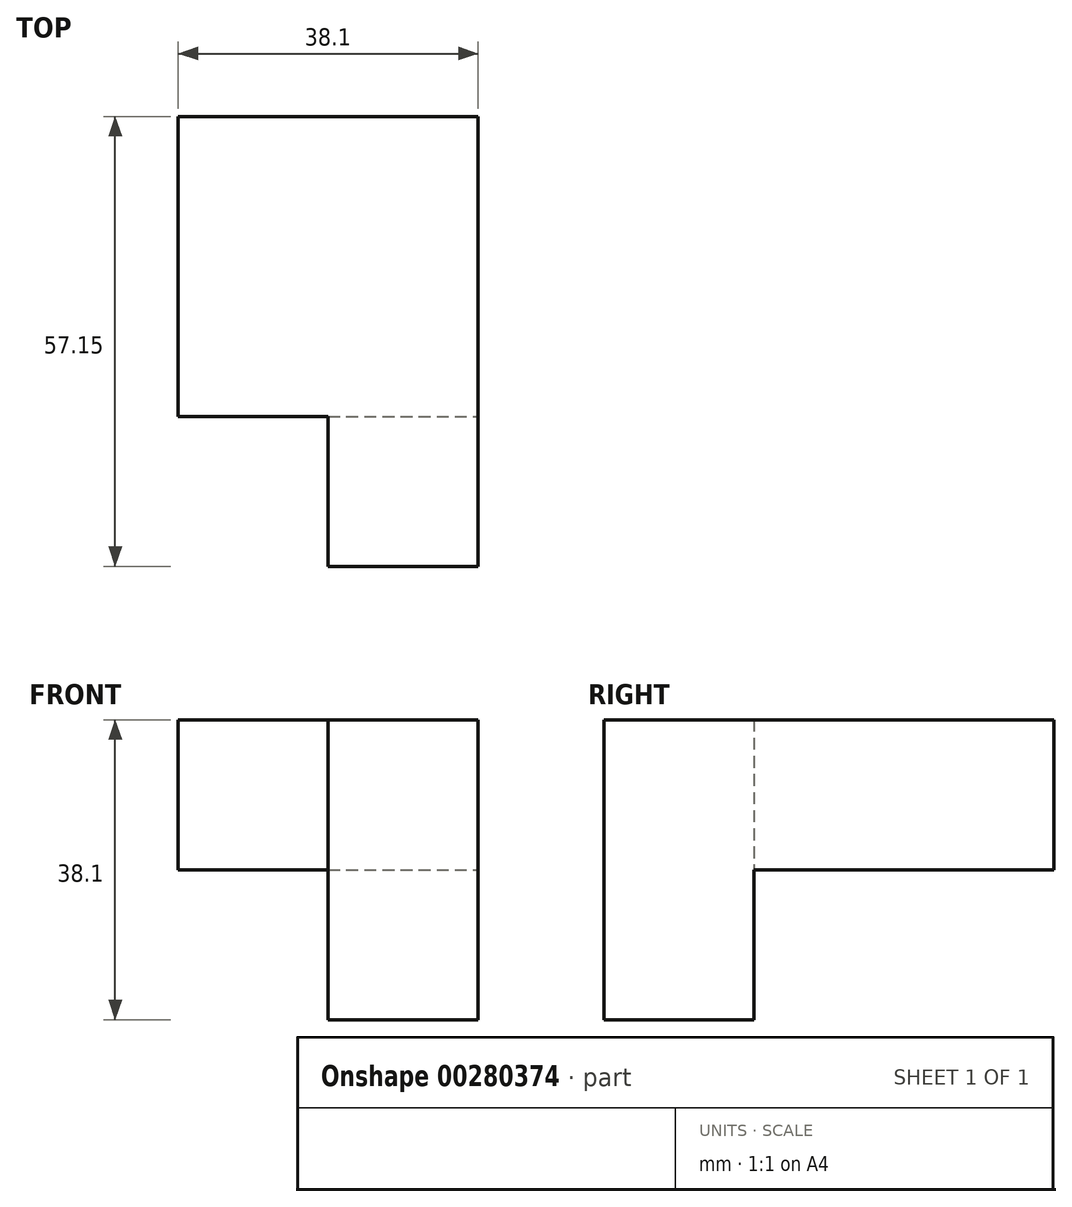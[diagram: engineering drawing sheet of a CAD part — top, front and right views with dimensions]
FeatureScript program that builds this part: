
annotation { "Feature Type Name" : "Feature", "Feature Type Description" : "" }
export const myFeature = defineFeature(function(context is Context, id is Id, definition is map)
    precondition{}
    {
        {
            var Q0;
            Q0=qCreatedBy(makeId("Top.planeOp"),FACE);
            var sketch = newSketch(context, id + "F0", { "sketchPlane" : qUnion([Q0])});
            skLineSegment(sketch, "E0.bottom", {"start": v(0, 0) * mm, "end": v(38.1, 0) * mm});
            skLineSegment(sketch, "E0.top", {"start": v(0, 38.1) * mm, "end": v(38.1, 38.1) * mm});
            skLineSegment(sketch, "E0.left", {"start": v(0, 0) * mm, "end": v(0, 38.1) * mm});
            skLineSegment(sketch, "E0.right", {"start": v(38.1, 0) * mm, "end": v(38.1, 38.1) * mm});
            skSolve(sketch);
        }
        {
            var Q0;
            Q0 = qSketchRegion(id + "F0", true);
            extrude(context, id + "F1", {"entities" : qUnion([Q0]), "depth" : 19.05 * mm});
        }
        {
            var Q0;
            Q0=makeQuery(id+"F1.opExtrude","SWEPT_FACE",FACE,{"disambiguationData":[OSD([sQuery(id+"F0.wireOp",EDGE,"E0.bottom")])]});
            var sketch = newSketch(context, id + "F2", { "sketchPlane" : qUnion([Q0])});
            skLineSegment(sketch, "E1.bottom", {"start": v(38.1, 19.05) * mm, "end": v(19.05, 19.05) * mm});
            skLineSegment(sketch, "E1.top", {"start": v(38.1, 0) * mm, "end": v(19.05, 0) * mm});
            skLineSegment(sketch, "E1.left", {"start": v(38.1, 19.05) * mm, "end": v(38.1, 0) * mm});
            skLineSegment(sketch, "E1.right", {"start": v(19.05, 19.05) * mm, "end": v(19.05, 0) * mm});
            skSolve(sketch);
        }
        {
            var Q0;
            Q0 = qSketchRegion(id + "F2", true);
            extrude(context, id + "F3", {"entities" : qUnion([Q0]), "operationType" : NewBodyOperationType.ADD, "depth" : 19.05 * mm});
        }
        {
            var Q0;
            Q0=makeQuery(id+"F3.boolean.opBoolean","MERGE",FACE,{"derivedFrom":[makeQuery(id+"F1.opExtrude","CAP_FACE",FACE,{"disambiguationData":[OSD([sQuery(id+"F0.wireOp",EDGE,"E0.bottom"),sQuery(id+"F0.wireOp",EDGE,"E0.top"),sQuery(id+"F0.wireOp",EDGE,"E0.left"),sQuery(id+"F0.wireOp",EDGE,"E0.right")])],"isStart":true}),makeQuery(id+"F3.opExtrude","SWEPT_FACE",FACE,{"disambiguationData":[OSD([sQuery(id+"F2.wireOp",EDGE,"E1.top")])]})]});
            var sketch = newSketch(context, id + "F4", { "sketchPlane" : qUnion([Q0])});
            skLineSegment(sketch, "E2.bottom", {"start": v(19.05, 19.05) * mm, "end": v(38.1, 19.05) * mm});
            skLineSegment(sketch, "E2.top", {"start": v(19.05, 0) * mm, "end": v(38.1, 0) * mm});
            skLineSegment(sketch, "E2.left", {"start": v(19.05, 19.05) * mm, "end": v(19.05, 0) * mm});
            skLineSegment(sketch, "E2.right", {"start": v(38.1, 19.05) * mm, "end": v(38.1, 0) * mm});
            skSolve(sketch);
        }
        {
            var Q0;
            Q0 = qSketchRegion(id + "F4", true);
            extrude(context, id + "F5", {"entities" : qUnion([Q0]), "operationType" : NewBodyOperationType.ADD, "depth" : 19.05 * mm});
        }
    });
